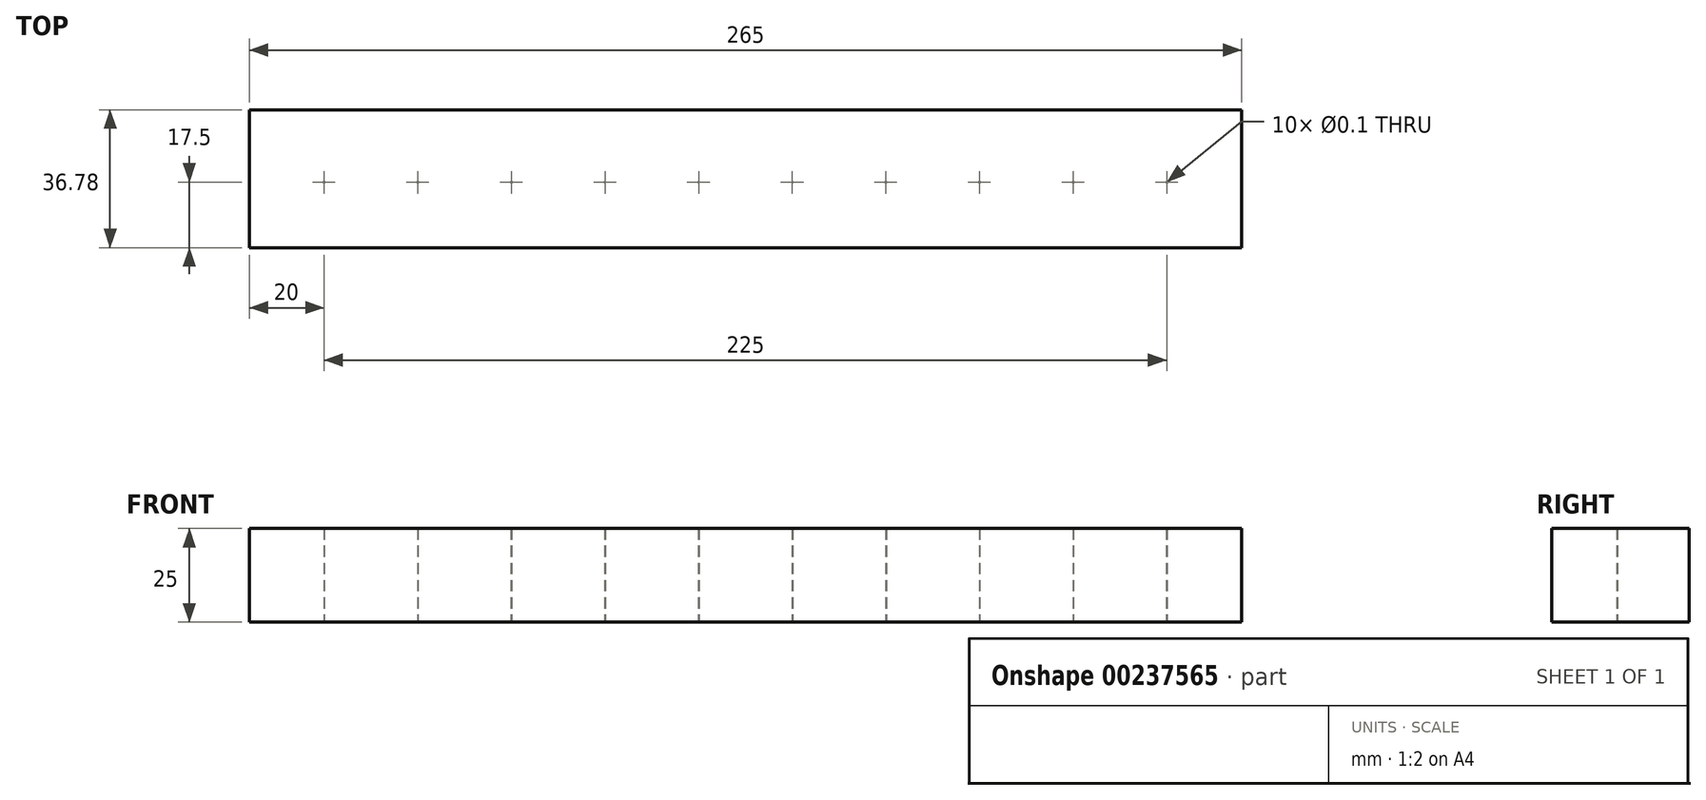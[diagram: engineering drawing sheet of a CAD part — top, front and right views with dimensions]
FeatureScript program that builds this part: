
annotation { "Feature Type Name" : "Feature", "Feature Type Description" : "" }
export const myFeature = defineFeature(function(context is Context, id is Id, definition is map)
    precondition{}
    {
        {
            var Q0;
            Q0=qCreatedBy(makeId("Top.planeOp"),FACE);
            var sketch = newSketch(context, id + "F0", { "sketchPlane" : qUnion([Q0])});
            skCircle(sketch, "E0", {"center": v(0, 0) * mm, "radius": 9.78 * mm, "construction": true});
            skCircle(sketch, "E1", {"center": v(0, 0) * mm, "radius": 0.05 * mm});
            skCircle(sketch, "E2.0.1.0", {"center": v(0, 35) * mm, "radius": 9.78 * mm, "construction": true});
            skCircle(sketch, "E2.0.1.1", {"center": v(0, 35) * mm, "radius": 0.05 * mm});
            skCircle(sketch, "E2.0.2.0", {"center": v(0, 70) * mm, "radius": 9.78 * mm, "construction": true});
            skCircle(sketch, "E2.0.2.1", {"center": v(0, 70) * mm, "radius": 0.05 * mm});
            skCircle(sketch, "E2.1.0.0", {"center": v(25, 0) * mm, "radius": 9.78 * mm, "construction": true});
            skCircle(sketch, "E2.1.0.1", {"center": v(25, 0) * mm, "radius": 0.05 * mm});
            skCircle(sketch, "E2.1.1.0", {"center": v(25, 35) * mm, "radius": 9.78 * mm, "construction": true});
            skCircle(sketch, "E2.1.1.1", {"center": v(25, 35) * mm, "radius": 0.05 * mm});
            skCircle(sketch, "E2.1.2.0", {"center": v(25, 70) * mm, "radius": 9.78 * mm, "construction": true});
            skCircle(sketch, "E2.1.2.1", {"center": v(25, 70) * mm, "radius": 0.05 * mm});
            skCircle(sketch, "E2.2.0.0", {"center": v(50, 0) * mm, "radius": 9.78 * mm, "construction": true});
            skCircle(sketch, "E2.2.0.1", {"center": v(50, 0) * mm, "radius": 0.05 * mm});
            skCircle(sketch, "E2.2.1.0", {"center": v(50, 35) * mm, "radius": 9.78 * mm, "construction": true});
            skCircle(sketch, "E2.2.1.1", {"center": v(50, 35) * mm, "radius": 0.05 * mm});
            skCircle(sketch, "E2.2.2.0", {"center": v(50, 70) * mm, "radius": 9.78 * mm, "construction": true});
            skCircle(sketch, "E2.2.2.1", {"center": v(50, 70) * mm, "radius": 0.05 * mm});
            skCircle(sketch, "E2.3.0.0", {"center": v(75, 0) * mm, "radius": 9.78 * mm, "construction": true});
            skCircle(sketch, "E2.3.0.1", {"center": v(75, 0) * mm, "radius": 0.05 * mm});
            skCircle(sketch, "E2.3.1.0", {"center": v(75, 35) * mm, "radius": 9.78 * mm, "construction": true});
            skCircle(sketch, "E2.3.1.1", {"center": v(75, 35) * mm, "radius": 0.05 * mm});
            skCircle(sketch, "E2.3.2.0", {"center": v(75, 70) * mm, "radius": 9.78 * mm, "construction": true});
            skCircle(sketch, "E2.3.2.1", {"center": v(75, 70) * mm, "radius": 0.05 * mm});
            skCircle(sketch, "E2.4.0.0", {"center": v(100, 0) * mm, "radius": 9.78 * mm, "construction": true});
            skCircle(sketch, "E2.4.0.1", {"center": v(100, 0) * mm, "radius": 0.05 * mm});
            skCircle(sketch, "E2.4.1.0", {"center": v(100, 35) * mm, "radius": 9.78 * mm, "construction": true});
            skCircle(sketch, "E2.4.1.1", {"center": v(100, 35) * mm, "radius": 0.05 * mm});
            skCircle(sketch, "E2.4.2.0", {"center": v(100, 70) * mm, "radius": 9.78 * mm, "construction": true});
            skCircle(sketch, "E2.4.2.1", {"center": v(100, 70) * mm, "radius": 0.05 * mm});
            skCircle(sketch, "E2.5.0.0", {"center": v(125, 0) * mm, "radius": 9.78 * mm, "construction": true});
            skCircle(sketch, "E2.5.0.1", {"center": v(125, 0) * mm, "radius": 0.05 * mm});
            skCircle(sketch, "E2.5.1.0", {"center": v(125, 35) * mm, "radius": 9.78 * mm, "construction": true});
            skCircle(sketch, "E2.5.1.1", {"center": v(125, 35) * mm, "radius": 0.05 * mm});
            skCircle(sketch, "E2.5.2.0", {"center": v(125, 70) * mm, "radius": 9.78 * mm, "construction": true});
            skCircle(sketch, "E2.5.2.1", {"center": v(125, 70) * mm, "radius": 0.05 * mm});
            skCircle(sketch, "E2.6.0.0", {"center": v(150, 0) * mm, "radius": 9.78 * mm, "construction": true});
            skCircle(sketch, "E2.6.0.1", {"center": v(150, 0) * mm, "radius": 0.05 * mm});
            skCircle(sketch, "E2.6.1.0", {"center": v(150, 35) * mm, "radius": 9.78 * mm, "construction": true});
            skCircle(sketch, "E2.6.1.1", {"center": v(150, 35) * mm, "radius": 0.05 * mm});
            skCircle(sketch, "E2.6.2.0", {"center": v(150, 70) * mm, "radius": 9.78 * mm, "construction": true});
            skCircle(sketch, "E2.6.2.1", {"center": v(150, 70) * mm, "radius": 0.05 * mm});
            skCircle(sketch, "E2.7.0.0", {"center": v(175, 0) * mm, "radius": 9.78 * mm, "construction": true});
            skCircle(sketch, "E2.7.0.1", {"center": v(175, 0) * mm, "radius": 0.05 * mm});
            skCircle(sketch, "E2.7.1.0", {"center": v(175, 35) * mm, "radius": 9.78 * mm, "construction": true});
            skCircle(sketch, "E2.7.1.1", {"center": v(175, 35) * mm, "radius": 0.05 * mm});
            skCircle(sketch, "E2.7.2.0", {"center": v(175, 70) * mm, "radius": 9.78 * mm, "construction": true});
            skCircle(sketch, "E2.7.2.1", {"center": v(175, 70) * mm, "radius": 0.05 * mm});
            skCircle(sketch, "E2.8.0.0", {"center": v(200, 0) * mm, "radius": 9.78 * mm, "construction": true});
            skCircle(sketch, "E2.8.0.1", {"center": v(200, 0) * mm, "radius": 0.05 * mm});
            skCircle(sketch, "E2.8.1.0", {"center": v(200, 35) * mm, "radius": 9.78 * mm, "construction": true});
            skCircle(sketch, "E2.8.1.1", {"center": v(200, 35) * mm, "radius": 0.05 * mm});
            skCircle(sketch, "E2.8.2.0", {"center": v(200, 70) * mm, "radius": 9.78 * mm, "construction": true});
            skCircle(sketch, "E2.8.2.1", {"center": v(200, 70) * mm, "radius": 0.05 * mm});
            skCircle(sketch, "E2.9.0.0", {"center": v(225, 0) * mm, "radius": 9.78 * mm, "construction": true});
            skCircle(sketch, "E2.9.0.1", {"center": v(225, 0) * mm, "radius": 0.05 * mm});
            skCircle(sketch, "E2.9.1.0", {"center": v(225, 35) * mm, "radius": 9.78 * mm, "construction": true});
            skCircle(sketch, "E2.9.1.1", {"center": v(225, 35) * mm, "radius": 0.05 * mm});
            skCircle(sketch, "E2.9.2.0", {"center": v(225, 70) * mm, "radius": 9.78 * mm, "construction": true});
            skCircle(sketch, "E2.9.2.1", {"center": v(225, 70) * mm, "radius": 0.05 * mm});
            skLineSegment(sketch, "E2.direction1", {"start": v(0, 0) * mm, "end": v(25, 0) * mm, "construction": true});
            skLineSegment(sketch, "E2.direction2", {"start": v(0, 0) * mm, "end": v(0, 35) * mm, "construction": true});
            skLineSegment(sketch, "E3.bottom", {"start": v(-20, -18) * mm, "end": v(245, -18) * mm});
            skLineSegment(sketch, "E3.top", {"start": v(-20, 89.28) * mm, "end": v(245, 89.28) * mm});
            skLineSegment(sketch, "E3.left", {"start": v(-20, -18) * mm, "end": v(-20, 89.28) * mm});
            skLineSegment(sketch, "E3.right", {"start": v(245, -18) * mm, "end": v(245, 89.28) * mm});
            skLineSegment(sketch, "E4", {"start": v(225, 70) * mm, "end": v(225, 35) * mm, "construction": true});
            skPoint(sketch, "E5.firstSnap0", {"position": v(0, 17.5) * mm});
            skLineSegment(sketch, "E5.bottom", {"start": v(-20, 17.5) * mm, "end": v(245, 17.5) * mm});
            skLineSegment(sketch, "E5.left", {"start": v(-20, 17.5) * mm, "end": v(-20, 89.28) * mm});
            skLineSegment(sketch, "E5.right", {"start": v(245, 17.5) * mm, "end": v(245, 89.28) * mm});
            skLineSegment(sketch, "E6", {"start": v(0, 70) * mm, "end": v(0, 35) * mm, "construction": true});
            skPoint(sketch, "E7.firstSnap0", {"position": v(0, 52.5) * mm});
            skLineSegment(sketch, "E7.bottom", {"start": v(-20, 52.5) * mm, "end": v(245, 52.5) * mm});
            skLineSegment(sketch, "E7.left", {"start": v(-20, 52.5) * mm, "end": v(-20, 89.28) * mm});
            skLineSegment(sketch, "E7.right", {"start": v(245, 52.5) * mm, "end": v(245, 89.28) * mm});
            skSolve(sketch);
        }
        {
            var Q0;
            Q0=makeQuery(id+"F0.imprint","IMPRINT",FACE,{"disambiguationData":[TD([[makeQuery(id+"F0.imprint","IMPRINT",EDGE,{"derivedFrom":sQuery(id+"F0.wireOp",EDGE,"E2.0.2.1")}),-1.0]])]});
            extrude(context, id + "F1", {"entities" : qUnion([Q0]), "depth" : 25 * mm});
        }
    });
